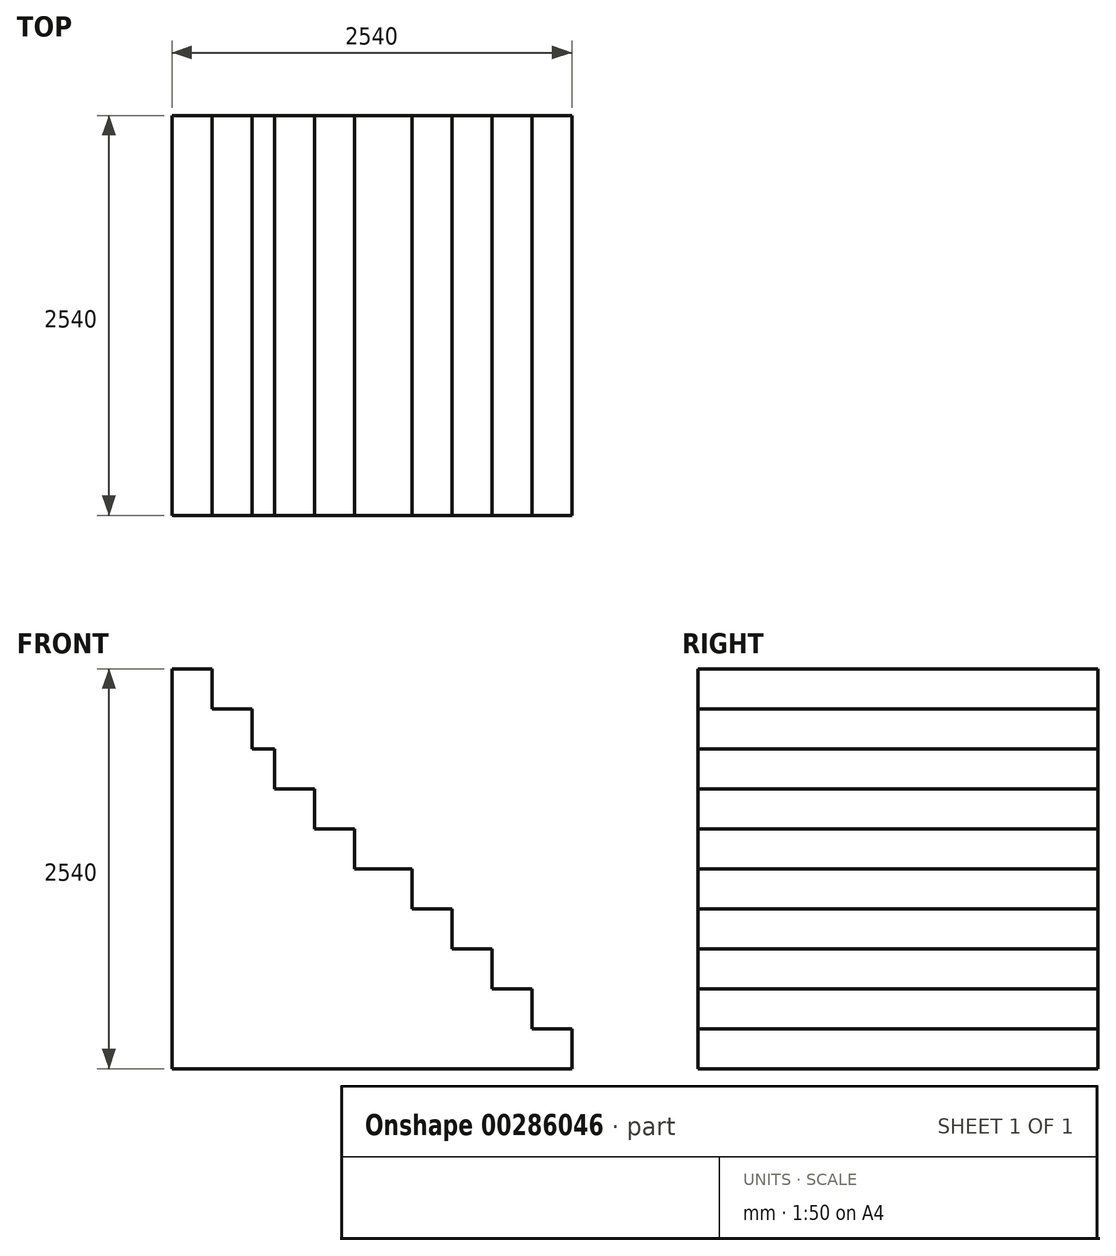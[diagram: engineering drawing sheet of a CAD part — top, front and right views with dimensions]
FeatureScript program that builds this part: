
annotation { "Feature Type Name" : "Feature", "Feature Type Description" : "" }
export const myFeature = defineFeature(function(context is Context, id is Id, definition is map)
    precondition{}
    {
        {
            var Q0;
            Q0=qCreatedBy(makeId("Front.planeOp"),FACE);
            var sketch = newSketch(context, id + "F0", { "sketchPlane" : qUnion([Q0])});
            skLineSegment(sketch, "E0", {"start": v(-882.79, 1763.08) * mm, "end": v(-628.79, 1763.08) * mm});
            skLineSegment(sketch, "E1", {"start": v(-628.79, 1763.08) * mm, "end": v(-628.79, 1509.08) * mm});
            skLineSegment(sketch, "E2", {"start": v(-628.79, 1509.08) * mm, "end": v(-374.79, 1509.08) * mm});
            skLineSegment(sketch, "E3", {"start": v(-374.79, 1509.08) * mm, "end": v(-374.79, 1255.08) * mm});
            skLineSegment(sketch, "E4", {"start": v(-374.79, 1255.08) * mm, "end": v(-231.43, 1255.08) * mm});
            skLineSegment(sketch, "E5", {"start": v(-231.43, 1255.08) * mm, "end": v(-231.43, 1001.08) * mm});
            skLineSegment(sketch, "E6", {"start": v(-231.43, 1001.08) * mm, "end": v(22.57, 1001.08) * mm});
            skLineSegment(sketch, "E7", {"start": v(22.57, 1001.08) * mm, "end": v(22.57, 747.08) * mm});
            skLineSegment(sketch, "E8", {"start": v(22.57, 747.08) * mm, "end": v(276.57, 747.08) * mm});
            skLineSegment(sketch, "E9", {"start": v(276.57, 747.08) * mm, "end": v(276.57, 493.08) * mm});
            skLineSegment(sketch, "E10", {"start": v(276.57, 493.08) * mm, "end": v(641.21, 493.08) * mm});
            skLineSegment(sketch, "E11", {"start": v(641.21, 493.08) * mm, "end": v(641.21, 239.08) * mm});
            skLineSegment(sketch, "E12", {"start": v(641.21, 239.08) * mm, "end": v(895.21, 239.08) * mm});
            skLineSegment(sketch, "E13", {"start": v(895.21, 239.08) * mm, "end": v(895.21, -14.92) * mm});
            skLineSegment(sketch, "E14", {"start": v(895.21, -14.92) * mm, "end": v(1149.21, -14.92) * mm});
            skLineSegment(sketch, "E15", {"start": v(1149.21, -14.92) * mm, "end": v(1149.21, -268.92) * mm});
            skLineSegment(sketch, "E16", {"start": v(1149.21, -268.92) * mm, "end": v(1403.21, -268.92) * mm});
            skLineSegment(sketch, "E17", {"start": v(1403.21, -268.92) * mm, "end": v(1403.21, -522.92) * mm});
            skLineSegment(sketch, "E18", {"start": v(1403.21, -522.92) * mm, "end": v(1657.21, -522.92) * mm});
            skLineSegment(sketch, "E19", {"start": v(1657.21, -522.92) * mm, "end": v(1657.21, -776.92) * mm});
            skLineSegment(sketch, "E20", {"start": v(-882.79, 1763.08) * mm, "end": v(-882.79, -776.92) * mm});
            skLineSegment(sketch, "E21", {"start": v(-882.79, -776.92) * mm, "end": v(1657.21, -776.92) * mm});
            skSolve(sketch);
        }
        {
            var Q0;
            Q0 = qSketchRegion(id + "F0", true);
            extrude(context, id + "F1", {"entities" : qUnion([Q0]), "depth" : 2540 * mm});
        }
    });
